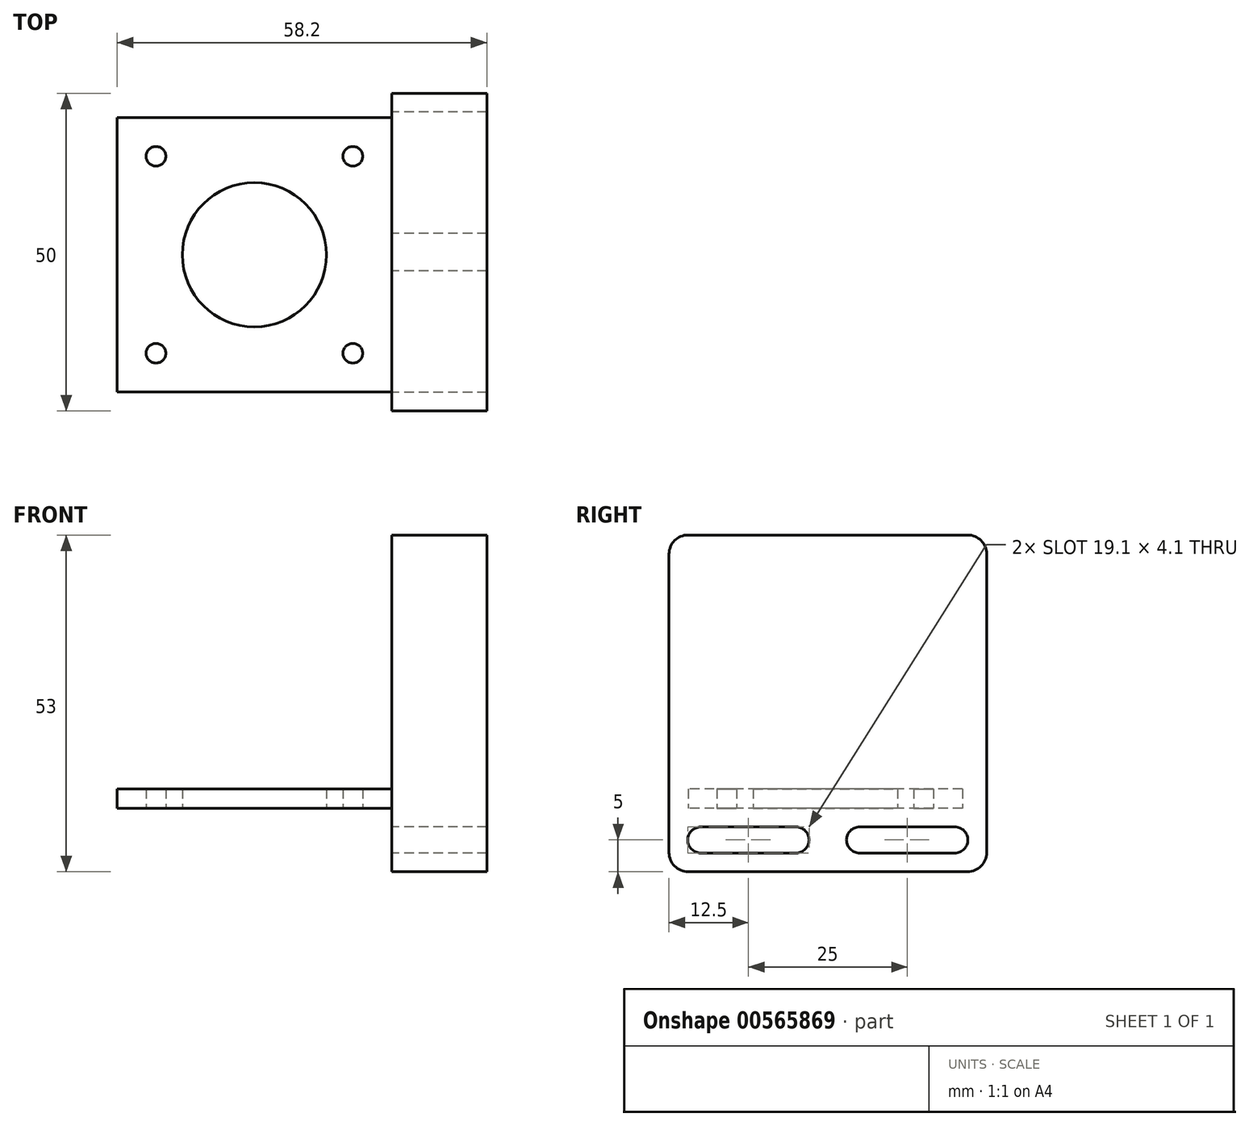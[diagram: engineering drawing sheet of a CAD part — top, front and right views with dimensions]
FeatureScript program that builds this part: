
annotation { "Feature Type Name" : "Feature", "Feature Type Description" : "" }
export const myFeature = defineFeature(function(context is Context, id is Id, definition is map)
    precondition{}
    {
        {
            var Q0;
            Q0=qCreatedBy(makeId("Top.planeOp"),FACE);
            var sketch = newSketch(context, id + "F0", { "sketchPlane" : qUnion([Q0])});
            skLineSegment(sketch, "E0.bottom", {"start": v(-21.6, 21.6) * mm, "end": v(21.6, 21.6) * mm});
            skLineSegment(sketch, "E0.top", {"start": v(-21.6, -21.6) * mm, "end": v(21.6, -21.6) * mm});
            skLineSegment(sketch, "E0.left", {"start": v(-21.6, 21.6) * mm, "end": v(-21.6, -21.6) * mm});
            skLineSegment(sketch, "E0.right", {"start": v(21.6, 21.6) * mm, "end": v(21.6, -21.6) * mm});
            skLineSegment(sketch, "E1", {"start": v(0, 21.6) * mm, "end": v(0, -21.6) * mm, "construction": true});
            skLineSegment(sketch, "E2", {"start": v(15.5, 21.6) * mm, "end": v(15.5, -21.6) * mm, "construction": true});
            skLineSegment(sketch, "E3", {"start": v(-15.5, 21.6) * mm, "end": v(-15.5, -21.6) * mm, "construction": true});
            skLineSegment(sketch, "E4", {"start": v(-21.6, 15.5) * mm, "end": v(21.6, 15.5) * mm, "construction": true});
            skLineSegment(sketch, "E5", {"start": v(-21.6, -15.5) * mm, "end": v(21.6, -15.5) * mm, "construction": true});
            skLineSegment(sketch, "E6", {"start": v(21.6, 0) * mm, "end": v(-21.6, 0) * mm, "construction": true});
            skCircle(sketch, "E7", {"center": v(0, 0) * mm, "radius": 11.35 * mm});
            skLineSegment(sketch, "E8", {"start": v(7, 15.5) * mm, "end": v(7, 0) * mm});
            skLineSegment(sketch, "E9", {"start": v(5.1, 0) * mm, "end": v(5.1, -15.5) * mm});
            skLineSegment(sketch, "E10", {"start": v(-15.5, 5.7) * mm, "end": v(0, 5.7) * mm});
            skLineSegment(sketch, "E11", {"start": v(0, 3.82) * mm, "end": v(15.5, 3.82) * mm});
            skCircle(sketch, "E12", {"center": v(-15.5, 15.5) * mm, "radius": 1.55 * mm});
            skCircle(sketch, "E13", {"center": v(15.5, 15.5) * mm, "radius": 1.55 * mm});
            skCircle(sketch, "E14", {"center": v(15.5, -15.5) * mm, "radius": 1.55 * mm});
            skCircle(sketch, "E15", {"center": v(-15.5, -15.5) * mm, "radius": 1.55 * mm});
            skSolve(sketch);
        }
        {
            var Q0;
            Q0=qSketchRegion(id+"F0",true);
            extrude(context, id + "F1", {"entities" : qUnion([Q0]), "depth" : 3 * mm});
        }
        {
            var Q0;
            Q0=makeQuery(id+"F1.opExtrude","SWEPT_FACE",FACE,{"disambiguationData":[OSD([sQuery(id+"F0.wireOp",EDGE,"E0.right")])]});
            var sketch = newSketch(context, id + "F2", { "sketchPlane" : qUnion([Q0])});
            skLineSegment(sketch, "E16.bottom", {"start": v(-24.6, 43) * mm, "end": v(25.4, 43) * mm});
            skLineSegment(sketch, "E16.top", {"start": v(-24.6, -10) * mm, "end": v(25.4, -10) * mm});
            skLineSegment(sketch, "E16.left", {"start": v(-24.6, 43) * mm, "end": v(-24.6, -10) * mm});
            skLineSegment(sketch, "E16.right", {"start": v(25.4, 43) * mm, "end": v(25.4, -10) * mm});
            skCircle(sketch, "E17", {"center": v(-19.6, -5) * mm, "radius": 2.05 * mm});
            skCircle(sketch, "E18", {"center": v(20.4, -5) * mm, "radius": 2.05 * mm});
            skLineSegment(sketch, "E19", {"start": v(-19.6, -2.95) * mm, "end": v(20.4, -2.95) * mm});
            skLineSegment(sketch, "E20", {"start": v(-19.6, -7.05) * mm, "end": v(20.4, -7.05) * mm});
            skArc(sketch, "E21", {"start": v(5.4, -2.95) * mm, "mid": v(3.35, -5) * mm, "end": v(5.4, -7.05) * mm});
            skArc(sketch, "E22", {"start": v(-4.6, -7.05) * mm, "mid": v(-2.55, -5) * mm, "end": v(-4.6, -2.95) * mm});
            skCircle(sketch, "E23", {"center": v(0, 0) * mm, "radius": 2.33 * mm});
            skSolve(sketch);
        }
        {
            var Q0;
            Q0=qSketchRegion(id+"F2",true);
            var Q1;
            {var subQ0=sQuery(id+"F2.wireOp",EDGE,"E21");Q1=makeQuery(id+"F2.imprint","IMPRINT",FACE,{"disambiguationData":[TD([[makeQuery(id+"F2.imprint","IMPRINT",EDGE,{"derivedFrom":subQ0}),-1.0]])]});}
            var Q2;
            {var subQ0=sQuery(id+"F2.wireOp",EDGE,"E23");var subQ1=makeQuery(id+"F1.opExtrude","CAP_EDGE",EDGE,{"disambiguationData":[OSD([sQuery(id+"F0.wireOp",EDGE,"E0.right")])],"isStart":true});var subQ2=makeQuery(id+"F2.imprint","INTERSECT",VERTEX,{"disambiguationData":[OD(0.0)],"derivedFrom":[subQ1,subQ0]});Q2=makeQuery(id+"F2.imprint","IMPRINT",FACE,{"disambiguationData":[TD([[makeQuery(id+"F2.imprint","IMPRINT",EDGE,{"disambiguationData":[TD([[subQ2,1.0]])],"derivedFrom":subQ0}),1.0]])]});}
            var Q3;
            {var subQ0=sQuery(id+"F2.wireOp",EDGE,"E23");var subQ1=makeQuery(id+"F1.opExtrude","CAP_EDGE",EDGE,{"disambiguationData":[OSD([sQuery(id+"F0.wireOp",EDGE,"E0.right")])],"isStart":true});var subQ2=makeQuery(id+"F2.imprint","INTERSECT",VERTEX,{"disambiguationData":[OD(0.0)],"derivedFrom":[subQ1,subQ0]});Q3=makeQuery(id+"F2.imprint","IMPRINT",FACE,{"disambiguationData":[TD([[makeQuery(id+"F2.imprint","IMPRINT",EDGE,{"disambiguationData":[TD([[subQ2,-1.0]])],"derivedFrom":subQ0}),1.0]])]});}
            extrude(context, id + "F3", {"entities" : qUnion([Q0, Q1, Q2, Q3]), "depth" : 15 * mm, "offsetDistance" : 25 * mm});
        }
        {
            var Q0;
            Q0=makeQuery(id+"F3.opExtrude","SWEPT_EDGE",EDGE,{"disambiguationData":[OSD([sQuery(id+"F2.wireOp",EDGE,"E16.top"),sQuery(id+"F2.wireOp",EDGE,"E16.right")])]});
            var Q1;
            Q1=makeQuery(id+"F3.opExtrude","SWEPT_EDGE",EDGE,{"disambiguationData":[OSD([sQuery(id+"F2.wireOp",EDGE,"E16.top"),sQuery(id+"F2.wireOp",EDGE,"E16.left")])]});
            var Q2;
            Q2=makeQuery(id+"FFNxEOOAgJ8R9Dv_2.opPattern","COPY",EDGE,{"derivedFrom":makeQuery(id+"FAvmf0ZsXksJTnV_1.opExtrude","CAP_EDGE",EDGE,{"disambiguationData":[OSD([sQuery(id+"F0.wireOp",EDGE,"E0.bottom")])],"isStart":false}),"instanceName":"1"});
            var Q3;
            Q3=makeQuery(id+"F3.opExtrude","SWEPT_EDGE",EDGE,{"disambiguationData":[OSD([sQuery(id+"F2.wireOp",EDGE,"E16.bottom"),sQuery(id+"F2.wireOp",EDGE,"E16.right")])]});
            var Q4;
            Q4=makeQuery(id+"F3.opExtrude","SWEPT_EDGE",EDGE,{"disambiguationData":[OSD([sQuery(id+"F2.wireOp",EDGE,"E16.bottom"),sQuery(id+"F2.wireOp",EDGE,"E16.left")])]});
            var Q5;
            Q5=makeQuery(id+"FFNxEOOAgJ8R9Dv_2.opPattern","COPY",EDGE,{"derivedFrom":makeQuery(id+"FAvmf0ZsXksJTnV_1.opExtrude","CAP_EDGE",EDGE,{"disambiguationData":[OSD([sQuery(id+"FGpwWgO6UiPWsFZ_1.wireOp",EDGE,"8SjgC7Pj-3DIV-6jF1-kdcX-FBYk4W7JzsZ4")])],"isStart":false}),"instanceName":"1"});
            var Q6;
            Q6=makeQuery(id+"FAvmf0ZsXksJTnV_1.opExtrude","CAP_EDGE",EDGE,{"disambiguationData":[OSD([sQuery(id+"FGpwWgO6UiPWsFZ_1.wireOp",EDGE,"8SjgC7Pj-3DIV-6jF1-kdcX-FBYk4W7JzsZ4")])],"isStart":false});
            var Q7;
            Q7=makeQuery(id+"FAvmf0ZsXksJTnV_1.opExtrude","CAP_EDGE",EDGE,{"disambiguationData":[OSD([sQuery(id+"F0.wireOp",EDGE,"E0.bottom")])],"isStart":false});
            fillet(context, id + "F4", {"entities" : qUnion([Q0, Q1, Q2, Q3, Q4, Q5, Q6, Q7]), "radius" : 3 * mm, "tangentPropagation" : true, "allowEdgeOverflow" : false});
        }
    });
